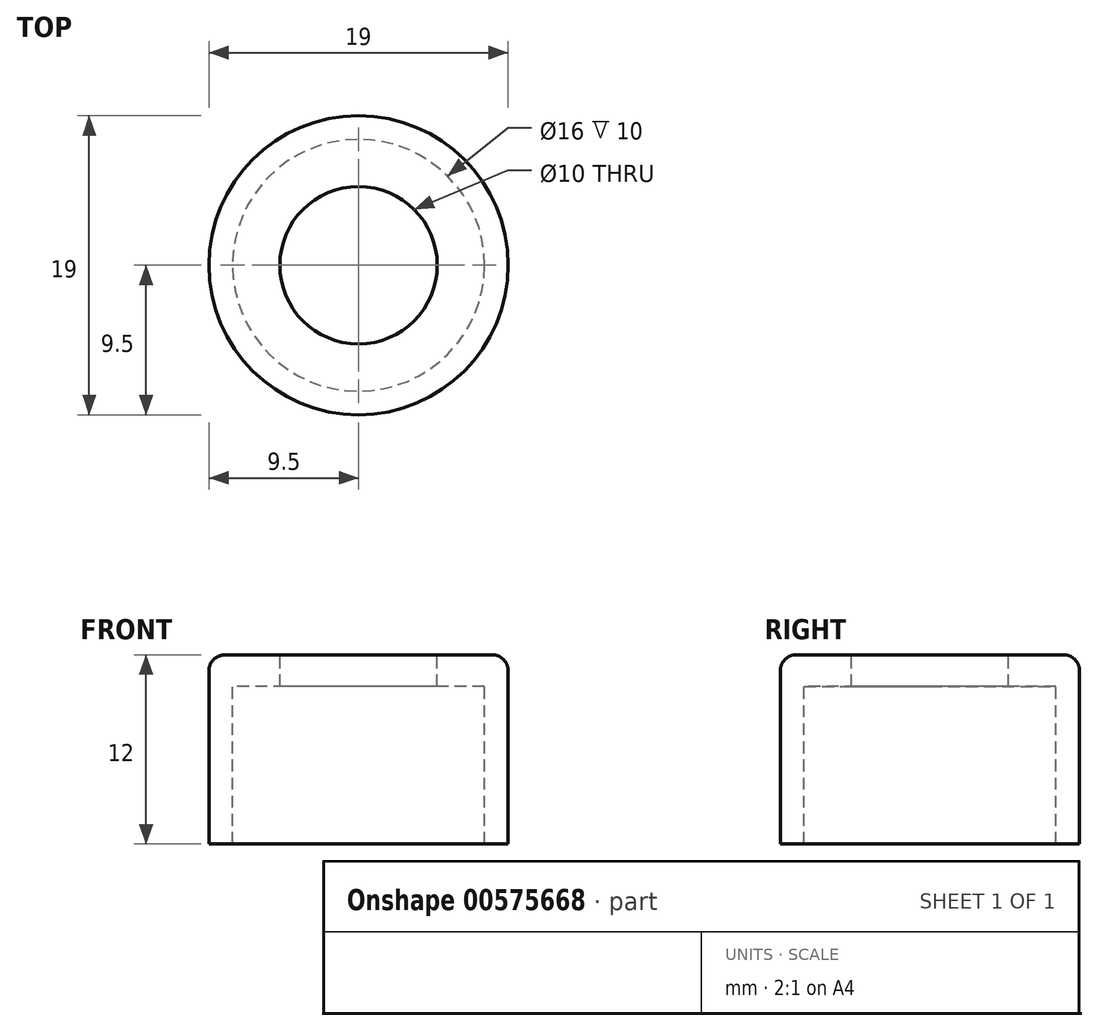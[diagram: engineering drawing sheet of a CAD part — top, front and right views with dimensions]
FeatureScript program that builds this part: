
annotation { "Feature Type Name" : "Feature", "Feature Type Description" : "" }
export const myFeature = defineFeature(function(context is Context, id is Id, definition is map)
    precondition{}
    {
        {
            var Q0;
            Q0=qCreatedBy(makeId("Front.planeOp"),FACE);
            var sketch = newSketch(context, id + "F0", { "sketchPlane" : qUnion([Q0])});
            skLineSegment(sketch, "E0.bottom", {"start": v(-8, 6) * mm, "end": v(-3.5, 6) * mm});
            skLineSegment(sketch, "E0.top", {"start": v(-8, -6) * mm, "end": v(-6.5, -6) * mm});
            skLineSegment(sketch, "E0.left", {"start": v(-8, 6) * mm, "end": v(-8, -6) * mm});
            skPoint(sketch, "E0.middle", {"position": v(0, 0) * mm});
            skLineSegment(sketch, "E1.left", {"start": v(-6.5, -6) * mm, "end": v(-6.5, 4) * mm});
            skLineSegment(sketch, "E2", {"start": v(-6.5, 4) * mm, "end": v(-3.5, 4) * mm});
            skLineSegment(sketch, "E3", {"start": v(1.5, 6) * mm, "end": v(1.5, 4) * mm, "construction": true});
            skLineSegment(sketch, "E4", {"start": v(-3.5, 6) * mm, "end": v(-3.5, 4) * mm});
            skSolve(sketch);
        }
        {
            var Q0;
            Q0=makeQuery(id+"F0.imprint","IMPRINT",FACE,{"disambiguationData":[TD([[makeQuery(id+"F0.imprint","IMPRINT",EDGE,{"derivedFrom":sQuery(id+"F0.wireOp",EDGE,"E0.bottom")}),-1.0]])]});
            var Q1;
            Q1=sQuery(id+"F0.wireOp",EDGE,"E3");
            revolve(context, id + "F1", {"entities" : qUnion([Q0]), "axis" : qUnion([Q1]), "revolveType" : RevolveType.FULL});
        }
        {
            var Q0;
            Q0=makeQuery(id+"F1.opRevolve","SWEPT_EDGE",EDGE,{"disambiguationData":[OSD([sQuery(id+"F0.wireOp",EDGE,"E0.bottom"),sQuery(id+"F0.wireOp",EDGE,"E0.left")])]});
            fillet(context, id + "F2", {"entities" : qUnion([Q0]), "radius" : 1 * mm, "tangentPropagation" : true, "allowEdgeOverflow" : false});
        }
    });
